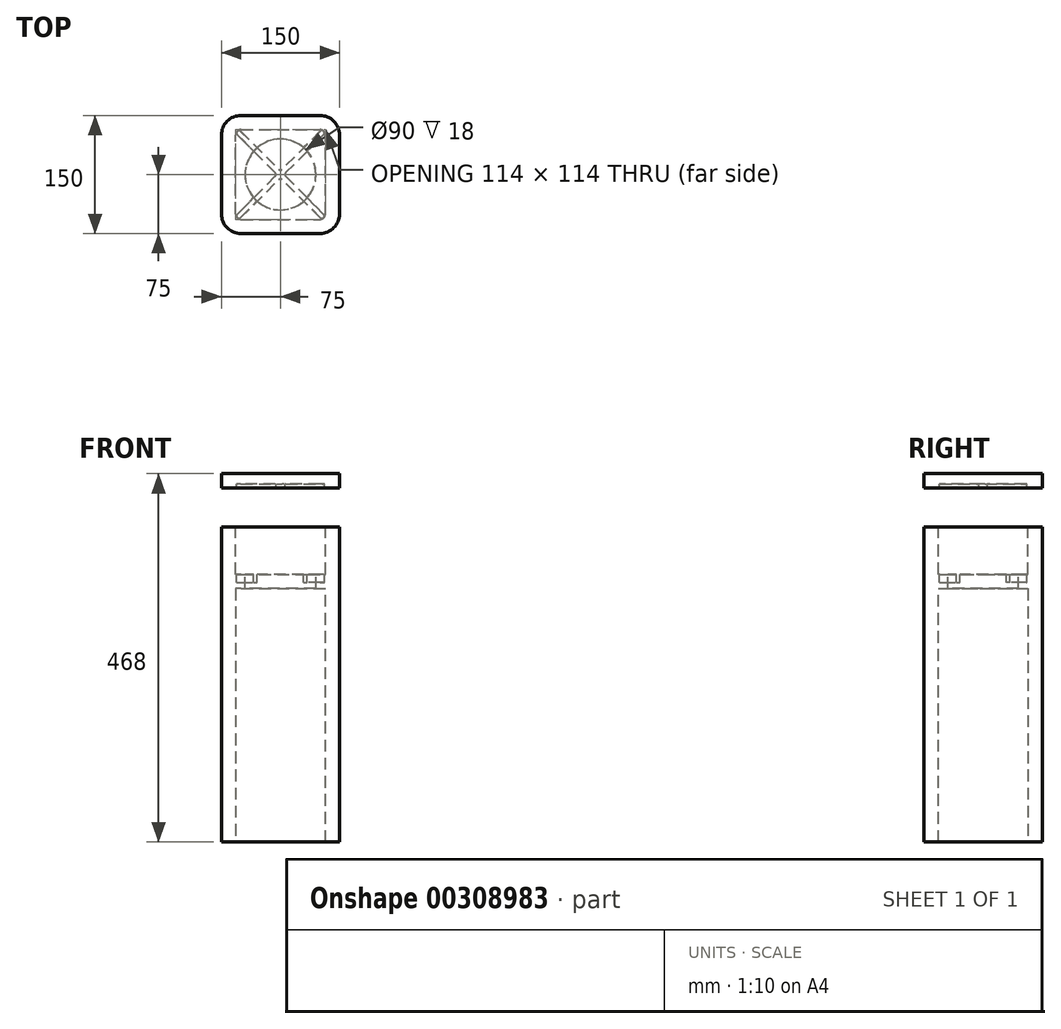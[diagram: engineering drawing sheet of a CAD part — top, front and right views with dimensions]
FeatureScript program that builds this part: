
annotation { "Feature Type Name" : "Feature", "Feature Type Description" : "" }
export const myFeature = defineFeature(function(context is Context, id is Id, definition is map)
    precondition{}
    {
        {
            var Q0;
            Q0=qCreatedBy(makeId("Top.planeOp"),FACE);
            var sketch = newSketch(context, id + "F0", { "sketchPlane" : qUnion([Q0])});
            skLineSegment(sketch, "E0", {"start": v(0, 75) * mm, "end": v(0, -75) * mm, "construction": true});
            skLineSegment(sketch, "E1", {"start": v(-75, 0) * mm, "end": v(75, 0) * mm, "construction": true});
            skLineSegment(sketch, "E2.bottom", {"start": v(-50, -75) * mm, "end": v(50, -75) * mm});
            skLineSegment(sketch, "E2.top", {"start": v(-50, 75) * mm, "end": v(50, 75) * mm});
            skLineSegment(sketch, "E2.left", {"start": v(-75, -50) * mm, "end": v(-75, 50) * mm});
            skLineSegment(sketch, "E2.right", {"start": v(75, -50) * mm, "end": v(75, 50) * mm});
            skPoint(sketch, "E3.visualSharp", {"position": v(-75, -75) * mm});
            skArc(sketch, "E3.filletArc", {"start": v(-75, -50) * mm, "mid": v(-67.68, -67.68) * mm, "end": v(-50, -75) * mm});
            skPoint(sketch, "E4.visualSharp", {"position": v(75, -75) * mm});
            skArc(sketch, "E4.filletArc", {"start": v(50, -75) * mm, "mid": v(67.68, -67.68) * mm, "end": v(75, -50) * mm});
            skPoint(sketch, "E5.visualSharp", {"position": v(75, 75) * mm});
            skArc(sketch, "E5.filletArc", {"start": v(75, 50) * mm, "mid": v(67.68, 67.68) * mm, "end": v(50, 75) * mm});
            skPoint(sketch, "E6.visualSharp", {"position": v(-75, 75) * mm});
            skArc(sketch, "E6.filletArc", {"start": v(-50, 75) * mm, "mid": v(-67.68, 67.68) * mm, "end": v(-75, 50) * mm});
            skSolve(sketch);
        }
        {
            var Q0;
            Q0=makeQuery(id+"F0.imprint","IMPRINT",FACE,{"disambiguationData":[TD([[makeQuery(id+"F0.imprint","IMPRINT",EDGE,{"derivedFrom":sQuery(id+"F0.wireOp",EDGE,"E2.bottom")}),1.0]])]});
            extrude(context, id + "F1", {"entities" : qUnion([Q0]), "depth" : 400 * mm});
        }
        {
            var Q0;
            Q0=makeQuery(id+"F1.opExtrude","CAP_FACE",FACE,{"disambiguationData":[OSD([sQuery(id+"F0.wireOp",EDGE,"E2.bottom"),sQuery(id+"F0.wireOp",EDGE,"E2.top"),sQuery(id+"F0.wireOp",EDGE,"E2.left"),sQuery(id+"F0.wireOp",EDGE,"E2.right"),sQuery(id+"F0.wireOp",EDGE,"E3.filletArc"),sQuery(id+"F0.wireOp",EDGE,"E4.filletArc"),sQuery(id+"F0.wireOp",EDGE,"E5.filletArc"),sQuery(id+"F0.wireOp",EDGE,"E6.filletArc")])],"isStart":false});
            var Q1;
            Q1=makeQuery(id+"F1.opExtrude","CAP_FACE",FACE,{"disambiguationData":[OSD([sQuery(id+"F0.wireOp",EDGE,"E2.bottom"),sQuery(id+"F0.wireOp",EDGE,"E2.top"),sQuery(id+"F0.wireOp",EDGE,"E2.left"),sQuery(id+"F0.wireOp",EDGE,"E2.right"),sQuery(id+"F0.wireOp",EDGE,"E3.filletArc"),sQuery(id+"F0.wireOp",EDGE,"E4.filletArc"),sQuery(id+"F0.wireOp",EDGE,"E5.filletArc"),sQuery(id+"F0.wireOp",EDGE,"E6.filletArc")])],"isStart":true});
            shell(context, id + "F2", {"entities" : qUnion([Q0, Q1]), "thickness" : 18 * mm});
        }
        {
            var Q0;
            Q0=makeQuery(id+"F1.opExtrude","CAP_FACE",FACE,{"disambiguationData":[OSD([sQuery(id+"F0.wireOp",EDGE,"E2.bottom"),sQuery(id+"F0.wireOp",EDGE,"E2.top"),sQuery(id+"F0.wireOp",EDGE,"E2.left"),sQuery(id+"F0.wireOp",EDGE,"E2.right"),sQuery(id+"F0.wireOp",EDGE,"E3.filletArc"),sQuery(id+"F0.wireOp",EDGE,"E4.filletArc"),sQuery(id+"F0.wireOp",EDGE,"E5.filletArc"),sQuery(id+"F0.wireOp",EDGE,"E6.filletArc")])],"isStart":false});
            cPlane(context, id + "F3", {"entities" : qUnion([Q0]), "cplaneType" : CPlaneType.OFFSET, "offset" : 50 * mm, "width" : 150 * mm, "height" : 150 * mm});
        }
        {
            var Q0;
            Q0=qCreatedBy(id+"F3.planeOp",FACE);
            var sketch = newSketch(context, id + "F4", { "sketchPlane" : qUnion([Q0])});
            skArc(sketch, "E7.0", {"start": v(-75, -50) * mm, "mid": v(-67.68, -67.68) * mm, "end": v(-50, -75) * mm});
            skLineSegment(sketch, "E8.0", {"start": v(-75, -50) * mm, "end": v(-75, 50) * mm});
            skArc(sketch, "E9.0", {"start": v(-50, 75) * mm, "mid": v(-67.68, 67.68) * mm, "end": v(-75, 50) * mm});
            skLineSegment(sketch, "E10.0", {"start": v(-50, 75) * mm, "end": v(50, 75) * mm});
            skArc(sketch, "E11.0", {"start": v(75, 50) * mm, "mid": v(67.68, 67.68) * mm, "end": v(50, 75) * mm});
            skLineSegment(sketch, "E12.0", {"start": v(75, -50) * mm, "end": v(75, 50) * mm});
            skArc(sketch, "E13.0", {"start": v(50, -75) * mm, "mid": v(67.68, -67.68) * mm, "end": v(75, -50) * mm});
            skLineSegment(sketch, "E14.0", {"start": v(-50, -75) * mm, "end": v(50, -75) * mm});
            skSolve(sketch);
        }
        {
            var Q0;
            Q0=makeQuery(id+"F4.imprint","IMPRINT",FACE,{"disambiguationData":[TD([[makeQuery(id+"F4.imprint","IMPRINT",EDGE,{"derivedFrom":sQuery(id+"F4.wireOp",EDGE,"E7.0")}),1.0]])]});
            extrude(context, id + "F5", {"entities" : qUnion([Q0]), "depth" : 18 * mm});
        }
        {
            var Q0;
            Q0=makeQuery(id+"F1.opExtrude","CAP_FACE",FACE,{"disambiguationData":[OSD([sQuery(id+"F0.wireOp",EDGE,"E2.bottom"),sQuery(id+"F0.wireOp",EDGE,"E2.top"),sQuery(id+"F0.wireOp",EDGE,"E2.left"),sQuery(id+"F0.wireOp",EDGE,"E2.right"),sQuery(id+"F0.wireOp",EDGE,"E3.filletArc"),sQuery(id+"F0.wireOp",EDGE,"E4.filletArc"),sQuery(id+"F0.wireOp",EDGE,"E5.filletArc"),sQuery(id+"F0.wireOp",EDGE,"E6.filletArc")])],"isStart":false});
            cPlane(context, id + "F6", {"entities" : qUnion([Q0]), "cplaneType" : CPlaneType.OFFSET, "offset" : 60 * mm, "oppositeDirection" : true, "width" : 150 * mm, "height" : 150 * mm});
        }
        {
            var Q0;
            Q0=qCreatedBy(id+"F6.planeOp",FACE);
            var sketch = newSketch(context, id + "F7", { "sketchPlane" : qUnion([Q0])});
            skLineSegment(sketch, "E15.0", {"start": v(-57, -50) * mm, "end": v(-57, 50) * mm});
            skArc(sketch, "E16.0", {"start": v(-50, 57) * mm, "mid": v(-54.95, 54.95) * mm, "end": v(-57, 50) * mm});
            skLineSegment(sketch, "E17.0", {"start": v(-50, 57) * mm, "end": v(50, 57) * mm});
            skArc(sketch, "E18.0", {"start": v(-57, -50) * mm, "mid": v(-54.95, -54.95) * mm, "end": v(-50, -57) * mm});
            skLineSegment(sketch, "E19.0", {"start": v(-50, -57) * mm, "end": v(50, -57) * mm});
            skArc(sketch, "E20.0", {"start": v(50, -57) * mm, "mid": v(54.95, -54.95) * mm, "end": v(57, -50) * mm});
            skLineSegment(sketch, "E21.0", {"start": v(57, -50) * mm, "end": v(57, 50) * mm});
            skArc(sketch, "E22.0", {"start": v(57, 50) * mm, "mid": v(54.95, 54.95) * mm, "end": v(50, 57) * mm});
            skCircle(sketch, "E23", {"center": v(0, 0) * mm, "radius": 45 * mm});
            skLineSegment(sketch, "E24", {"start": v(-57, 0) * mm, "end": v(0, 0) * mm, "construction": true});
            skLineSegment(sketch, "E25", {"start": v(0, 57) * mm, "end": v(0, 0) * mm, "construction": true});
            skSolve(sketch);
        }
        {
            var Q0;
            Q0=makeQuery(id+"F7.imprint","IMPRINT",FACE,{"disambiguationData":[TD([[makeQuery(id+"F7.imprint","IMPRINT",EDGE,{"derivedFrom":sQuery(id+"F7.wireOp",EDGE,"E15.0")}),-1.0]])]});
            extrude(context, id + "F8", {"entities" : qUnion([Q0]), "operationType" : NewBodyOperationType.ADD, "oppositeDirection" : true, "depth" : 18 * mm});
        }
        {
            var Q0;
            Q0=makeQuery(id+"F8.opExtrude","CAP_FACE",FACE,{"disambiguationData":[OSD([sQuery(id+"F7.wireOp",EDGE,"E15.0"),sQuery(id+"F7.wireOp",EDGE,"E16.0"),sQuery(id+"F7.wireOp",EDGE,"E17.0"),sQuery(id+"F7.wireOp",EDGE,"E18.0"),sQuery(id+"F7.wireOp",EDGE,"E19.0"),sQuery(id+"F7.wireOp",EDGE,"E20.0"),sQuery(id+"F7.wireOp",EDGE,"E21.0"),sQuery(id+"F7.wireOp",EDGE,"E22.0"),sQuery(id+"F7.wireOp",EDGE,"E23")])],"isStart":true});
            var sketch = newSketch(context, id + "F9", { "sketchPlane" : qUnion([Q0])});
            skArc(sketch, "E26.0", {"start": v(-50, 57) * mm, "mid": v(-54.95, 54.95) * mm, "end": v(-57, 50) * mm, "construction": true});
            skArc(sketch, "E27.0", {"start": v(33.94, 29.55) * mm, "mid": v(31.82, 31.82) * mm, "end": v(29.55, 33.94) * mm});
            skLineSegment(sketch, "E28", {"start": v(-54.95, 54.95) * mm, "end": v(66.26, -66.26) * mm, "construction": true});
            skLineSegment(sketch, "E29", {"start": v(54.95, 54.95) * mm, "end": v(-54.95, -54.95) * mm, "construction": true});
            skLineSegment(sketch, "E30.0", {"start": v(-57.14, 52.76) * mm, "end": v(-56.63, 52.25) * mm});
            skLineSegment(sketch, "E31.0", {"start": v(-52.76, 57.14) * mm, "end": v(-52.25, 56.63) * mm});
            skArc(sketch, "E32", {"start": v(-50.57, 54.95) * mm, "mid": v(-54.95, 54.95) * mm, "end": v(-54.95, 50.57) * mm});
            skLineSegment(sketch, "E33.trimOffspring", {"start": v(-54.95, 50.57) * mm, "end": v(-33.94, 29.55) * mm});
            skLineSegment(sketch, "E34.trimOffspring", {"start": v(-50.57, 54.95) * mm, "end": v(-29.55, 33.94) * mm});
            skLineSegment(sketch, "E35.MirrorCS", {"start": v(54.95, 50.57) * mm, "end": v(33.94, 29.55) * mm});
            skLineSegment(sketch, "E36.MirrorCS", {"start": v(50.57, 54.95) * mm, "end": v(29.55, 33.94) * mm});
            skArc(sketch, "E37.MirrorCS", {"start": v(50.57, 54.95) * mm, "mid": v(54.95, 54.95) * mm, "end": v(54.95, 50.57) * mm});
            skArc(sketch, "E38.MirrorC", {"start": v(-33.94, 29.55) * mm, "mid": v(-31.82, 31.82) * mm, "end": v(-29.55, 33.94) * mm});
            skArc(sketch, "E39.trimOffspring", {"start": v(-31.82, -31.82) * mm, "mid": v(0, -45) * mm, "end": v(31.82, -31.82) * mm});
            skArc(sketch, "E40.trimOffspring", {"start": v(-29.55, 33.94) * mm, "mid": v(-31.82, 31.82) * mm, "end": v(-33.94, 29.55) * mm});
            skLineSegment(sketch, "E41.MirrorCS", {"start": v(-54.95, -50.57) * mm, "end": v(-33.94, -29.55) * mm});
            skLineSegment(sketch, "E42.MirrorCS", {"start": v(-50.57, -54.95) * mm, "end": v(-29.55, -33.94) * mm});
            skArc(sketch, "E43.MirrorCS", {"start": v(-50.57, -54.95) * mm, "mid": v(-54.95, -54.95) * mm, "end": v(-54.95, -50.57) * mm});
            skArc(sketch, "E44.MirrorCS", {"start": v(-33.94, -29.55) * mm, "mid": v(-31.82, -31.82) * mm, "end": v(-29.55, -33.94) * mm});
            skArc(sketch, "E45.MirrorCS", {"start": v(33.94, -29.55) * mm, "mid": v(31.82, -31.82) * mm, "end": v(29.55, -33.94) * mm});
            skLineSegment(sketch, "E46.MirrorCS", {"start": v(50.57, -54.95) * mm, "end": v(29.55, -33.94) * mm});
            skLineSegment(sketch, "E47.MirrorCS", {"start": v(54.95, -50.57) * mm, "end": v(33.94, -29.55) * mm});
            skArc(sketch, "E48.MirrorCS", {"start": v(50.57, -54.95) * mm, "mid": v(54.95, -54.95) * mm, "end": v(54.95, -50.57) * mm});
            skSolve(sketch);
        }
        {
            var Q0;
            {var subQ1=sQuery(id+"F9.wireOp",EDGE,"E46.MirrorCS");Q0=makeQuery(id+"F9.imprint","IMPRINT",FACE,{"disambiguationData":[TD([[makeQuery(id+"F9.imprint","IMPRINT",EDGE,{"derivedFrom":subQ1}),-1.0]])]});}
            var Q1;
            {var subQ1=sQuery(id+"F9.wireOp",EDGE,"E41.MirrorCS");Q1=makeQuery(id+"F9.imprint","IMPRINT",FACE,{"disambiguationData":[TD([[makeQuery(id+"F9.imprint","IMPRINT",EDGE,{"derivedFrom":subQ1}),-1.0]])]});}
            var Q2;
            {var subQ1=sQuery(id+"F9.wireOp",EDGE,"E33.trimOffspring");Q2=makeQuery(id+"F9.imprint","IMPRINT",FACE,{"disambiguationData":[TD([[makeQuery(id+"F9.imprint","IMPRINT",EDGE,{"derivedFrom":subQ1}),1.0]])]});}
            var Q3;
            Q3=makeQuery(id+"F9.imprint","IMPRINT",FACE,{"disambiguationData":[TD([[makeQuery(id+"F9.imprint","IMPRINT",EDGE,{"derivedFrom":sQuery(id+"F9.wireOp",EDGE,"E27.0")}),-1.0]])]});
            extrude(context, id + "F10", {"entities" : qUnion([Q0, Q1, Q2, Q3]), "operationType" : NewBodyOperationType.REMOVE, "oppositeDirection" : true, "depth" : 10 * mm});
        }
        {
            var Q0;
            Q0=makeQuery(id+"F5.opExtrude","CAP_FACE",FACE,{"disambiguationData":[OSD([sQuery(id+"F4.wireOp",EDGE,"E7.0"),sQuery(id+"F4.wireOp",EDGE,"E8.0"),sQuery(id+"F4.wireOp",EDGE,"E9.0"),sQuery(id+"F4.wireOp",EDGE,"E10.0"),sQuery(id+"F4.wireOp",EDGE,"E11.0"),sQuery(id+"F4.wireOp",EDGE,"E12.0"),sQuery(id+"F4.wireOp",EDGE,"E13.0"),sQuery(id+"F4.wireOp",EDGE,"E14.0")])],"isStart":true});
            var sketch = newSketch(context, id + "F11", { "sketchPlane" : qUnion([Q0])});
            skLineSegment(sketch, "E49", {"start": v(-52.6, 57) * mm, "end": v(0, 4.38) * mm});
            skLineSegment(sketch, "E50", {"start": v(57, -52.6) * mm, "end": v(52.6, -57) * mm});
            skLineSegment(sketch, "E51", {"start": v(52.6, -57) * mm, "end": v(0, -4.38) * mm});
            skLineSegment(sketch, "E52", {"start": v(-57, 52.6) * mm, "end": v(-52.6, 57) * mm});
            skLineSegment(sketch, "E53", {"start": v(-54.8, 54.8) * mm, "end": v(54.8, -54.8) * mm, "construction": true});
            skLineSegment(sketch, "E54", {"start": v(-75, 0) * mm, "end": v(0, 0) * mm, "construction": true});
            skPoint(sketch, "E54.endSnap0", {"position": v(-75, 0) * mm});
            skLineSegment(sketch, "E55", {"start": v(0, 0) * mm, "end": v(0, 75) * mm, "construction": true});
            skLineSegment(sketch, "E56.MirrorCS", {"start": v(52.6, 57) * mm, "end": v(0, 4.38) * mm});
            skLineSegment(sketch, "E57.MirrorCS", {"start": v(-52.6, -57) * mm, "end": v(0, -4.38) * mm});
            skLineSegment(sketch, "E58.MirrorCS", {"start": v(-57, -52.6) * mm, "end": v(-52.6, -57) * mm});
            skLineSegment(sketch, "E59.MirrorCS", {"start": v(57, 52.6) * mm, "end": v(52.6, 57) * mm});
            skLineSegment(sketch, "E60.trimOffspring", {"start": v(-4.38, 0) * mm, "end": v(-57, 52.6) * mm});
            skLineSegment(sketch, "E61.trimOffspring", {"start": v(4.38, 0) * mm, "end": v(57, 52.6) * mm});
            skLineSegment(sketch, "E62.trimOffspring", {"start": v(4.38, 0) * mm, "end": v(57, -52.6) * mm});
            skLineSegment(sketch, "E63.trimOffspring", {"start": v(-4.38, 0) * mm, "end": v(-57, -52.6) * mm});
            skSolve(sketch);
        }
        {
            var Q0;
            Q0=makeQuery(id+"F11.imprint","IMPRINT",FACE,{"disambiguationData":[TD([[makeQuery(id+"F11.imprint","IMPRINT",EDGE,{"derivedFrom":sQuery(id+"F11.wireOp",EDGE,"E49")}),-1.0]])]});
            extrude(context, id + "F12", {"entities" : qUnion([Q0]), "operationType" : NewBodyOperationType.REMOVE, "oppositeDirection" : true, "depth" : 5 * mm});
        }
        {
            var Q0;
            Q0=makeQuery(id+"F12.boolean.opBoolean","COPY",EDGE,{"derivedFrom":makeQuery(id+"F12.opExtrude","SWEPT_EDGE",EDGE,{"disambiguationData":[OSD([sQuery(id+"F11.wireOp",EDGE,"E49"),sQuery(id+"F11.wireOp",EDGE,"E52")])]})});
            var Q1;
            Q1=makeQuery(id+"F12.boolean.opBoolean","COPY",EDGE,{"derivedFrom":makeQuery(id+"F12.opExtrude","SWEPT_EDGE",EDGE,{"disambiguationData":[OSD([sQuery(id+"F11.wireOp",EDGE,"E52"),sQuery(id+"F11.wireOp",EDGE,"E60.trimOffspring")])]})});
            var Q2;
            Q2=makeQuery(id+"F12.boolean.opBoolean","COPY",EDGE,{"derivedFrom":makeQuery(id+"F12.opExtrude","SWEPT_EDGE",EDGE,{"disambiguationData":[OSD([sQuery(id+"F11.wireOp",EDGE,"E58.MirrorCS"),sQuery(id+"F11.wireOp",EDGE,"E63.trimOffspring")])]})});
            var Q3;
            Q3=makeQuery(id+"F12.boolean.opBoolean","COPY",EDGE,{"derivedFrom":makeQuery(id+"F12.opExtrude","SWEPT_EDGE",EDGE,{"disambiguationData":[OSD([sQuery(id+"F11.wireOp",EDGE,"E57.MirrorCS"),sQuery(id+"F11.wireOp",EDGE,"E58.MirrorCS")])]})});
            var Q4;
            Q4=makeQuery(id+"F12.boolean.opBoolean","COPY",EDGE,{"derivedFrom":makeQuery(id+"F12.opExtrude","SWEPT_EDGE",EDGE,{"disambiguationData":[OSD([sQuery(id+"F11.wireOp",EDGE,"E50"),sQuery(id+"F11.wireOp",EDGE,"E51")])]})});
            var Q5;
            Q5=makeQuery(id+"F12.boolean.opBoolean","COPY",EDGE,{"derivedFrom":makeQuery(id+"F12.opExtrude","SWEPT_EDGE",EDGE,{"disambiguationData":[OSD([sQuery(id+"F11.wireOp",EDGE,"E50"),sQuery(id+"F11.wireOp",EDGE,"E62.trimOffspring")])]})});
            var Q6;
            Q6=makeQuery(id+"F12.boolean.opBoolean","COPY",EDGE,{"derivedFrom":makeQuery(id+"F12.opExtrude","SWEPT_EDGE",EDGE,{"disambiguationData":[OSD([sQuery(id+"F11.wireOp",EDGE,"E59.MirrorCS"),sQuery(id+"F11.wireOp",EDGE,"E61.trimOffspring")])]})});
            var Q7;
            Q7=makeQuery(id+"F12.boolean.opBoolean","COPY",EDGE,{"derivedFrom":makeQuery(id+"F12.opExtrude","SWEPT_EDGE",EDGE,{"disambiguationData":[OSD([sQuery(id+"F11.wireOp",EDGE,"E56.MirrorCS"),sQuery(id+"F11.wireOp",EDGE,"E59.MirrorCS")])]})});
            var Q8;
            Q8=makeQuery(id+"F12.boolean.opBoolean","COPY",EDGE,{"derivedFrom":makeQuery(id+"F12.opExtrude","SWEPT_EDGE",EDGE,{"disambiguationData":[OSD([sQuery(id+"F11.wireOp",EDGE,"E49"),sQuery(id+"F11.wireOp",EDGE,"E56.MirrorCS")])]})});
            var Q9;
            Q9=makeQuery(id+"F12.boolean.opBoolean","COPY",EDGE,{"derivedFrom":makeQuery(id+"F12.opExtrude","SWEPT_EDGE",EDGE,{"disambiguationData":[OSD([sQuery(id+"F11.wireOp",EDGE,"E61.trimOffspring"),sQuery(id+"F11.wireOp",EDGE,"E62.trimOffspring")])]})});
            var Q10;
            Q10=makeQuery(id+"F12.boolean.opBoolean","COPY",EDGE,{"derivedFrom":makeQuery(id+"F12.opExtrude","SWEPT_EDGE",EDGE,{"disambiguationData":[OSD([sQuery(id+"F11.wireOp",EDGE,"E51"),sQuery(id+"F11.wireOp",EDGE,"E57.MirrorCS")])]})});
            var Q11;
            Q11=makeQuery(id+"F12.boolean.opBoolean","COPY",EDGE,{"derivedFrom":makeQuery(id+"F12.opExtrude","SWEPT_EDGE",EDGE,{"disambiguationData":[OSD([sQuery(id+"F11.wireOp",EDGE,"E60.trimOffspring"),sQuery(id+"F11.wireOp",EDGE,"E63.trimOffspring")])]})});
            fillet(context, id + "F13", {"entities" : qUnion([Q0, Q1, Q2, Q3, Q4, Q5, Q6, Q7, Q8, Q9, Q10, Q11]), "radius" : (6.2 / 2) * mm, "tangentPropagation" : true, "allowEdgeOverflow" : false});
        }
    });
